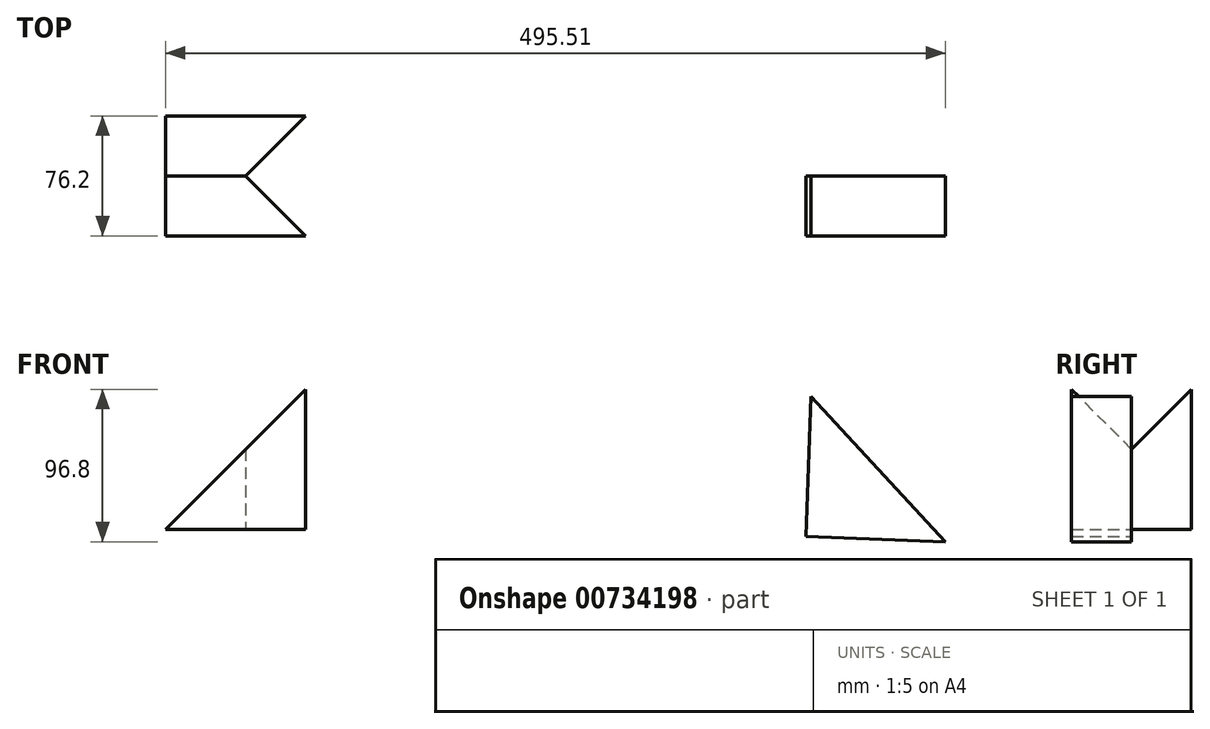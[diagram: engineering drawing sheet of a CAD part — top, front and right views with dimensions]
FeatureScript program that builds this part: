
annotation { "Feature Type Name" : "Feature", "Feature Type Description" : "" }
export const myFeature = defineFeature(function(context is Context, id is Id, definition is map)
    precondition{}
    {
        {
            var Q0;
            Q0=qCreatedBy(makeId("Front.planeOp"),FACE);
            var sketch = newSketch(context, id + "F0", { "sketchPlane" : qUnion([Q0])});
            skLineSegment(sketch, "E0", {"start": v(66.82, 257.53) * mm, "end": v(155.72, 257.53) * mm});
            skLineSegment(sketch, "E1", {"start": v(155.72, 257.53) * mm, "end": v(155.72, 346.43) * mm});
            skLineSegment(sketch, "E2", {"start": v(155.72, 346.43) * mm, "end": v(66.82, 257.53) * mm});
            skSolve(sketch);
        }
        {
            var Q0;
            Q0=makeQuery(id+"F0.imprint","IMPRINT",FACE,{"disambiguationData":[TD([[makeQuery(id+"F0.imprint","IMPRINT",EDGE,{"derivedFrom":sQuery(id+"F0.wireOp",EDGE,"E0")}),1.0]])]});
            extrude(context, id + "F1", {"entities" : qUnion([Q0]), "depth" : 38.1 * mm, "offsetDistance" : 25.4 * mm});
        }
        {
            var Q0;
            Q0=qCreatedBy(makeId("Front.planeOp"),FACE);
            var sketch = newSketch(context, id + "F2", { "sketchPlane" : qUnion([Q0])});
            skLineSegment(sketch, "E3", {"start": v(219.24, 257.56) * mm, "end": v(205.65, 358.25) * mm});
            skLineSegment(sketch, "E4", {"start": v(205.65, 358.25) * mm, "end": v(319.93, 271.16) * mm});
            skLineSegment(sketch, "E5", {"start": v(319.93, 271.16) * mm, "end": v(219.24, 257.56) * mm});
            skSolve(sketch);
        }
        {
            var Q0;
            Q0 = qSketchRegion(id + "F2", true);
            extrude(context, id + "F3", {"entities" : qUnion([Q0]), "depth" : 38.1 * mm, "offsetDistance" : 25.4 * mm});
        }
        {
            var Q0;
            Q0=qCreatedBy(makeId("Front.planeOp"),FACE);
            var sketch = newSketch(context, id + "F4", { "sketchPlane" : qUnion([Q0])});
            skLineSegment(sketch, "E6", {"start": v(476.84, 341.81) * mm, "end": v(473.49, 252.98) * mm});
            skLineSegment(sketch, "E7", {"start": v(473.49, 252.98) * mm, "end": v(562.33, 249.63) * mm});
            skLineSegment(sketch, "E8", {"start": v(562.33, 249.63) * mm, "end": v(476.84, 341.81) * mm});
            skSolve(sketch);
        }
        {
            var Q0;
            Q0 = qSketchRegion(id + "F4", true);
            extrude(context, id + "F5", {"entities" : qUnion([Q0]), "depth" : 38.1 * mm, "offsetDistance" : 25.4 * mm});
        }
        {
            var Q0;
            Q0=makeQuery(id+"F3.opExtrude","SWEPT_FACE",FACE,{"disambiguationData":[OSD([sQuery(id+"F2.wireOp",EDGE,"E5")])]});
            var sketch = newSketch(context, id + "F6", { "sketchPlane" : qUnion([Q0])});
            skLineSegment(sketch, "E9", {"start": v(251.75, 38.1) * mm, "end": v(289.85, 0) * mm});
            skLineSegment(sketch, "E10", {"start": v(289.85, 0) * mm, "end": v(251.75, 0) * mm});
            skLineSegment(sketch, "E11", {"start": v(251.75, 0) * mm, "end": v(251.75, 38.1) * mm});
            skSolve(sketch);
        }
        {
            var Q0;
            Q0=makeQuery(id+"F6.imprint","IMPRINT",FACE,{"disambiguationData":[TD([[makeQuery(id+"F6.imprint","IMPRINT",EDGE,{"derivedFrom":sQuery(id+"F6.wireOp",EDGE,"E9")}),-1.0]])]});
            extrude(context, id + "F7", {"entities" : qUnion([Q0]), "operationType" : NewBodyOperationType.REMOVE, "endBound" : BoundingType.THROUGH_ALL, "oppositeDirection" : true, "depth" : 25.4 * mm, "offsetDistance" : 25.4 * mm});
        }
        {
            var Q0;
            Q0=makeQuery(id+"F1.opExtrude","SWEPT_FACE",FACE,{"disambiguationData":[OSD([sQuery(id+"F0.wireOp",EDGE,"E0")])]});
            var sketch = newSketch(context, id + "F8", { "sketchPlane" : qUnion([Q0])});
            skLineSegment(sketch, "E12", {"start": v(155.72, 38.1) * mm, "end": v(155.72, 0) * mm});
            skLineSegment(sketch, "E13", {"start": v(155.72, 0) * mm, "end": v(117.62, 0) * mm});
            skLineSegment(sketch, "E14", {"start": v(117.62, 0) * mm, "end": v(155.72, 38.1) * mm});
            skSolve(sketch);
        }
        {
            var Q0;
            Q0 = qSketchRegion(id + "F8", true);
            extrude(context, id + "F9", {"entities" : qUnion([Q0]), "operationType" : NewBodyOperationType.REMOVE, "endBound" : BoundingType.THROUGH_ALL, "oppositeDirection" : true, "depth" : 25.4 * mm, "offsetDistance" : 25.4 * mm});
        }
        {
            var Q0;
            Q0=makeQuery(id+"F3.opExtrude","SWEPT_BODY",BODY,{"disambiguationData":[OSD([sQuery(id+"F2.wireOp",EDGE,"E3"),sQuery(id+"F2.wireOp",EDGE,"E4"),sQuery(id+"F2.wireOp",EDGE,"E5")])]});
            deleteBodies(context, id + "F10", {"entities" : qUnion([Q0])});
        }
        {
            var Q0;
            Q0=makeQuery(id+"F1.opExtrude","SWEPT_BODY",BODY,{"disambiguationData":[OSD([sQuery(id+"F0.wireOp",EDGE,"E0"),sQuery(id+"F0.wireOp",EDGE,"E1"),sQuery(id+"F0.wireOp",EDGE,"E2")])]});
            var Q1;
            Q1=qCreatedBy(makeId("Front.planeOp"),FACE);
            mirror(context, id + "F11", {"entities" : qUnion([Q0]), "mirrorPlane" : qUnion([Q1])});
        }
    });
